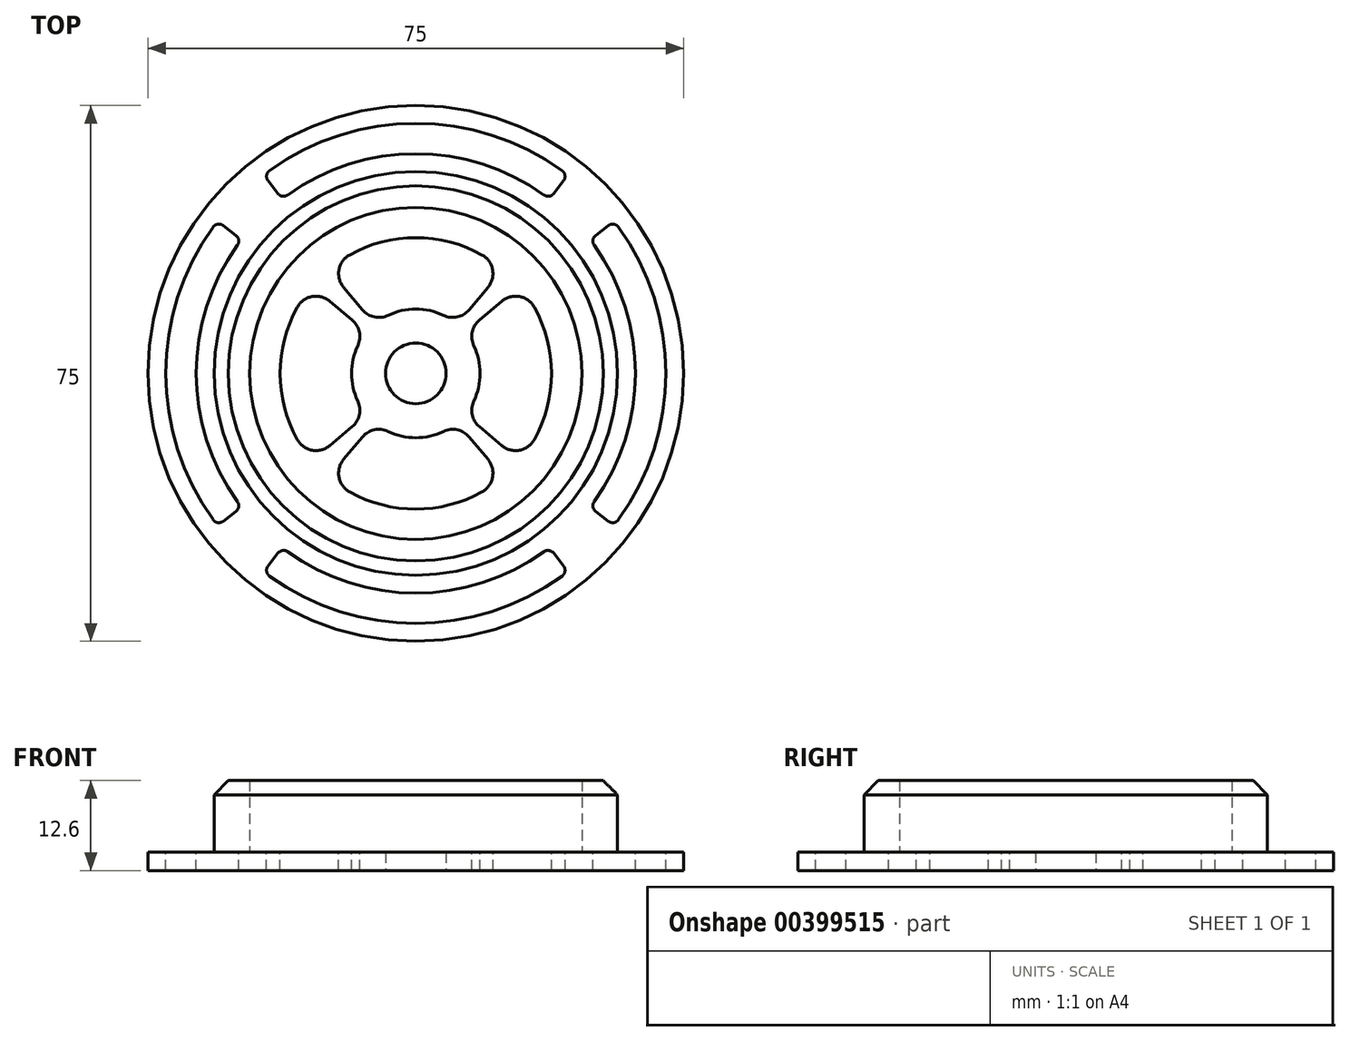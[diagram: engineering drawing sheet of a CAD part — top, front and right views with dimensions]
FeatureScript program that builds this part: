
annotation { "Feature Type Name" : "Feature", "Feature Type Description" : "" }
export const myFeature = defineFeature(function(context is Context, id is Id, definition is map)
    precondition{}
    {
        {
            var Q0;
            Q0=qCreatedBy(makeId("Top.planeOp"),FACE);
            var sketch = newSketch(context, id + "F0", { "sketchPlane" : qUnion([Q0])});
            skCircle(sketch, "E0", {"center": v(0, 0) * mm, "radius": 37.5 * mm});
            skCircle(sketch, "E1", {"center": v(0, 0) * mm, "radius": 23.25 * mm});
            skSolve(sketch);
        }
        {
            var Q0;
            Q0=makeQuery(id+"F0.imprint","IMPRINT",FACE,{"disambiguationData":[TD([[makeQuery(id+"F0.imprint","IMPRINT",EDGE,{"derivedFrom":sQuery(id+"F0.wireOp",EDGE,"E0")}),1.0]])]});
            extrude(context, id + "F1", {"entities" : qUnion([Q0]), "depth" : 2.6 * mm});
        }
        {
            var Q0;
            Q0=makeQuery(id+"F1.opExtrude","CAP_FACE",FACE,{"disambiguationData":[OSD([sQuery(id+"F0.wireOp",EDGE,"E0"),sQuery(id+"F0.wireOp",EDGE,"E1")])],"isStart":false});
            var sketch = newSketch(context, id + "F2", { "sketchPlane" : qUnion([Q0])});
            skCircle(sketch, "E2", {"center": v(0, 0) * mm, "radius": 28.25 * mm});
            skCircle(sketch, "E3", {"center": v(0, 0) * mm, "radius": 23.25 * mm});
            skSolve(sketch);
        }
        {
            var Q0;
            Q0=makeQuery(id+"F2.imprint","IMPRINT",FACE,{"disambiguationData":[TD([[makeQuery(id+"F2.imprint","IMPRINT",EDGE,{"derivedFrom":sQuery(id+"F2.wireOp",EDGE,"E2")}),1.0]])]});
            extrude(context, id + "F3", {"entities" : qUnion([Q0]), "operationType" : NewBodyOperationType.ADD, "depth" : 10 * mm});
        }
        {
            var Q0;
            Q0=makeQuery(id+"F3.opExtrude","CAP_EDGE",EDGE,{"disambiguationData":[OSD([sQuery(id+"F2.wireOp",EDGE,"E2")])],"isStart":false});
            chamfer(context, id + "F4", {"entities" : qUnion([Q0]), "width" : 2 * mm, "tangentPropagation" : true});
        }
        {
            var Q0;
            Q0=qCreatedBy(makeId("Top.planeOp"),FACE);
            var sketch = newSketch(context, id + "F5", { "sketchPlane" : qUnion([Q0])});
            skCircle(sketch, "E4", {"center": v(0, 0) * mm, "radius": 4.25 * mm});
            skCircle(sketch, "E5", {"center": v(0, 0) * mm, "radius": 23.25 * mm});
            skSolve(sketch);
        }
        {
            var Q0;
            Q0=makeQuery(id+"F5.imprint","IMPRINT",FACE,{"disambiguationData":[TD([[makeQuery(id+"F5.imprint","IMPRINT",EDGE,{"derivedFrom":sQuery(id+"F5.wireOp",EDGE,"E4")}),-1.0]])]});
            extrude(context, id + "F6", {"entities" : qUnion([Q0]), "operationType" : NewBodyOperationType.ADD, "depth" : 2.6 * mm});
        }
        {
            var Q0;
            Q0=makeQuery(id+"F6.opExtrude","CAP_FACE",FACE,{"disambiguationData":[OSD([sQuery(id+"F5.wireOp",EDGE,"E4"),sQuery(id+"F5.wireOp",EDGE,"E5")])],"isStart":false});
            var sketch = newSketch(context, id + "F7", { "sketchPlane" : qUnion([Q0])});
            skArc(sketch, "E6", {"start": v(3.88, 8.12) * mm, "mid": v(0, 9) * mm, "end": v(-3.88, 8.12) * mm});
            skArc(sketch, "E7", {"start": v(9.27, 16.59) * mm, "mid": v(0, 19) * mm, "end": v(-9.27, 16.59) * mm});
            skLineSegment(sketch, "E8", {"start": v(-7.47, 8.9) * mm, "end": v(-10.1, 12.04) * mm});
            skLineSegment(sketch, "E9", {"start": v(7.47, 8.9) * mm, "end": v(10.1, 12.04) * mm});
            skPoint(sketch, "E10.visualSharp", {"position": v(-12.21, 14.55) * mm});
            skArc(sketch, "E10.filletArc", {"start": v(-11.98, 14.75) * mm, "mid": v(-12.09, 14.54) * mm, "end": v(-12.02, 14.32) * mm});
            skArc(sketch, "E11.filletArc", {"start": v(-9.27, 16.59) * mm, "mid": v(-10.75, 14.5) * mm, "end": v(-10.1, 12.04) * mm});
            skPoint(sketch, "E12.visualSharp", {"position": v(-5.79, 6.9) * mm});
            skArc(sketch, "E12.filletArc", {"start": v(-7.47, 8.9) * mm, "mid": v(-5.8, 7.9) * mm, "end": v(-3.88, 8.12) * mm});
            skPoint(sketch, "E13.visualSharp", {"position": v(5.79, 6.9) * mm});
            skArc(sketch, "E13.filletArc", {"start": v(3.88, 8.12) * mm, "mid": v(5.8, 7.9) * mm, "end": v(7.47, 8.9) * mm});
            skPoint(sketch, "E14.visualSharp", {"position": v(12.21, 14.55) * mm});
            skArc(sketch, "E14.filletArc", {"start": v(10.1, 12.04) * mm, "mid": v(10.75, 14.5) * mm, "end": v(9.27, 16.59) * mm});
            skPoint(sketch, "E15.1.0", {"position": v(-6.9, -5.79) * mm});
            skArc(sketch, "E15.1.1", {"start": v(-12.04, 10.1) * mm, "mid": v(-14.5, 10.75) * mm, "end": v(-16.59, 9.27) * mm});
            skPoint(sketch, "E15.1.2", {"position": v(-14.55, 12.21) * mm});
            skPoint(sketch, "E15.1.3", {"position": v(-14.55, -12.21) * mm});
            skArc(sketch, "E15.1.4", {"start": v(-16.59, -9.27) * mm, "mid": v(-14.5, -10.75) * mm, "end": v(-12.04, -10.1) * mm});
            skArc(sketch, "E15.1.5", {"start": v(-8.12, 3.88) * mm, "mid": v(-9, 0) * mm, "end": v(-8.12, -3.88) * mm});
            skPoint(sketch, "E15.1.6", {"position": v(-6.9, 5.79) * mm});
            skArc(sketch, "E15.1.7", {"start": v(-16.59, 9.27) * mm, "mid": v(-19, 0) * mm, "end": v(-16.59, -9.27) * mm});
            skLineSegment(sketch, "E15.1.8", {"start": v(-8.9, 7.47) * mm, "end": v(-12.04, 10.1) * mm});
            skLineSegment(sketch, "E15.1.9", {"start": v(-8.9, -7.47) * mm, "end": v(-12.04, -10.1) * mm});
            skArc(sketch, "E15.1.10", {"start": v(-8.12, 3.88) * mm, "mid": v(-7.9, 5.8) * mm, "end": v(-8.9, 7.47) * mm});
            skArc(sketch, "E15.1.11", {"start": v(-8.9, -7.47) * mm, "mid": v(-7.9, -5.8) * mm, "end": v(-8.12, -3.88) * mm});
            skArc(sketch, "E15.1.12", {"start": v(-14.75, -11.98) * mm, "mid": v(-14.54, -12.09) * mm, "end": v(-14.32, -12.02) * mm});
            skPoint(sketch, "E15.2.0", {"position": v(5.79, -6.9) * mm});
            skArc(sketch, "E15.2.1", {"start": v(-10.1, -12.04) * mm, "mid": v(-10.75, -14.5) * mm, "end": v(-9.27, -16.59) * mm});
            skPoint(sketch, "E15.2.2", {"position": v(-12.21, -14.55) * mm});
            skPoint(sketch, "E15.2.3", {"position": v(12.21, -14.55) * mm});
            skArc(sketch, "E15.2.4", {"start": v(9.27, -16.59) * mm, "mid": v(10.75, -14.5) * mm, "end": v(10.1, -12.04) * mm});
            skArc(sketch, "E15.2.5", {"start": v(-3.88, -8.12) * mm, "mid": v(0, -9) * mm, "end": v(3.88, -8.12) * mm});
            skPoint(sketch, "E15.2.6", {"position": v(-5.79, -6.9) * mm});
            skArc(sketch, "E15.2.7", {"start": v(-9.27, -16.59) * mm, "mid": v(0, -19) * mm, "end": v(9.27, -16.59) * mm});
            skLineSegment(sketch, "E15.2.8", {"start": v(-7.47, -8.9) * mm, "end": v(-10.1, -12.04) * mm});
            skLineSegment(sketch, "E15.2.9", {"start": v(7.47, -8.9) * mm, "end": v(10.1, -12.04) * mm});
            skArc(sketch, "E15.2.10", {"start": v(-3.88, -8.12) * mm, "mid": v(-5.8, -7.9) * mm, "end": v(-7.47, -8.9) * mm});
            skArc(sketch, "E15.2.11", {"start": v(7.47, -8.9) * mm, "mid": v(5.8, -7.9) * mm, "end": v(3.88, -8.12) * mm});
            skArc(sketch, "E15.2.12", {"start": v(11.98, -14.75) * mm, "mid": v(12.09, -14.54) * mm, "end": v(12.02, -14.32) * mm});
            skPoint(sketch, "E15.3.0", {"position": v(6.9, 5.79) * mm});
            skArc(sketch, "E15.3.1", {"start": v(12.04, -10.1) * mm, "mid": v(14.5, -10.75) * mm, "end": v(16.59, -9.27) * mm});
            skPoint(sketch, "E15.3.2", {"position": v(14.55, -12.21) * mm});
            skPoint(sketch, "E15.3.3", {"position": v(14.55, 12.21) * mm});
            skArc(sketch, "E15.3.4", {"start": v(16.59, 9.27) * mm, "mid": v(14.5, 10.75) * mm, "end": v(12.04, 10.1) * mm});
            skArc(sketch, "E15.3.5", {"start": v(8.12, -3.88) * mm, "mid": v(9, 0) * mm, "end": v(8.12, 3.88) * mm});
            skPoint(sketch, "E15.3.6", {"position": v(6.9, -5.79) * mm});
            skArc(sketch, "E15.3.7", {"start": v(16.59, -9.27) * mm, "mid": v(19, 0) * mm, "end": v(16.59, 9.27) * mm});
            skLineSegment(sketch, "E15.3.8", {"start": v(8.9, -7.47) * mm, "end": v(12.04, -10.1) * mm});
            skLineSegment(sketch, "E15.3.9", {"start": v(8.9, 7.47) * mm, "end": v(12.04, 10.1) * mm});
            skArc(sketch, "E15.3.10", {"start": v(8.12, -3.88) * mm, "mid": v(7.9, -5.8) * mm, "end": v(8.9, -7.47) * mm});
            skArc(sketch, "E15.3.11", {"start": v(8.9, 7.47) * mm, "mid": v(7.9, 5.8) * mm, "end": v(8.12, 3.88) * mm});
            skArc(sketch, "E15.3.12", {"start": v(14.75, 11.98) * mm, "mid": v(14.54, 12.09) * mm, "end": v(14.32, 12.02) * mm});
            skSolve(sketch);
        }
        {
            var Q0;
            Q0=makeQuery(id+"F7.imprint","IMPRINT",FACE,{"disambiguationData":[TD([[makeQuery(id+"F7.imprint","IMPRINT",EDGE,{"derivedFrom":sQuery(id+"F7.wireOp",EDGE,"E6")}),-1.0]])]});
            var Q1;
            Q1=makeQuery(id+"F7.imprint","IMPRINT",FACE,{"disambiguationData":[TD([[makeQuery(id+"F7.imprint","IMPRINT",EDGE,{"derivedFrom":sQuery(id+"F7.wireOp",EDGE,"E15.3.1")}),1.0]])]});
            var Q2;
            Q2=makeQuery(id+"F7.imprint","IMPRINT",FACE,{"disambiguationData":[TD([[makeQuery(id+"F7.imprint","IMPRINT",EDGE,{"derivedFrom":sQuery(id+"F7.wireOp",EDGE,"E15.2.1")}),1.0]])]});
            var Q3;
            Q3=makeQuery(id+"F7.imprint","IMPRINT",FACE,{"disambiguationData":[TD([[makeQuery(id+"F7.imprint","IMPRINT",EDGE,{"derivedFrom":sQuery(id+"F7.wireOp",EDGE,"E15.1.1")}),1.0]])]});
            extrude(context, id + "F8", {"entities" : qUnion([Q0, Q1, Q2, Q3]), "operationType" : NewBodyOperationType.REMOVE, "endBound" : BoundingType.THROUGH_ALL, "oppositeDirection" : true, "depth" : 25 * mm});
        }
        {
            var Q0;
            Q0=makeQuery(id+"F1.opExtrude","CAP_FACE",FACE,{"disambiguationData":[OSD([sQuery(id+"F0.wireOp",EDGE,"E0"),sQuery(id+"F0.wireOp",EDGE,"E1")])],"isStart":false});
            var sketch = newSketch(context, id + "F9", { "sketchPlane" : qUnion([Q0])});
            skArc(sketch, "E16", {"start": v(20.48, 28.38) * mm, "mid": v(0, 35) * mm, "end": v(-20.48, 28.38) * mm});
            skArc(sketch, "E17", {"start": v(17.94, 24.97) * mm, "mid": v(0, 30.75) * mm, "end": v(-17.94, 24.97) * mm});
            skLineSegment(sketch, "E18", {"start": v(-19.32, 25.18) * mm, "end": v(-20.69, 26.96) * mm});
            skLineSegment(sketch, "E19", {"start": v(19.32, 25.18) * mm, "end": v(20.69, 26.96) * mm});
            skPoint(sketch, "E20.visualSharp", {"position": v(-21.3, 27.77) * mm});
            skArc(sketch, "E20.filletArc", {"start": v(-20.48, 28.38) * mm, "mid": v(-20.88, 27.72) * mm, "end": v(-20.69, 26.96) * mm});
            skPoint(sketch, "E21.visualSharp", {"position": v(-18.72, 24.4) * mm});
            skArc(sketch, "E21.filletArc", {"start": v(-19.32, 25.18) * mm, "mid": v(-18.67, 24.8) * mm, "end": v(-17.94, 24.97) * mm});
            skPoint(sketch, "E22.visualSharp", {"position": v(18.72, 24.4) * mm});
            skArc(sketch, "E22.filletArc", {"start": v(17.94, 24.97) * mm, "mid": v(18.67, 24.8) * mm, "end": v(19.32, 25.18) * mm});
            skPoint(sketch, "E23.visualSharp", {"position": v(21.3, 27.77) * mm});
            skArc(sketch, "E23.filletArc", {"start": v(20.69, 26.96) * mm, "mid": v(20.88, 27.72) * mm, "end": v(20.48, 28.38) * mm});
            skPoint(sketch, "E24.1.0", {"position": v(-24.4, 18.72) * mm});
            skPoint(sketch, "E24.1.1", {"position": v(-24.4, -18.72) * mm});
            skPoint(sketch, "E24.1.2", {"position": v(-27.77, 21.3) * mm});
            skPoint(sketch, "E24.1.3", {"position": v(-27.77, -21.3) * mm});
            skArc(sketch, "E24.1.4", {"start": v(-28.38, 20.48) * mm, "mid": v(-35, 0) * mm, "end": v(-28.38, -20.48) * mm});
            skArc(sketch, "E24.1.5", {"start": v(-24.97, 17.94) * mm, "mid": v(-30.75, 0) * mm, "end": v(-24.97, -17.94) * mm});
            skArc(sketch, "E24.1.6", {"start": v(-25.18, -19.32) * mm, "mid": v(-24.8, -18.67) * mm, "end": v(-24.97, -17.94) * mm});
            skArc(sketch, "E24.1.7", {"start": v(-26.96, 20.69) * mm, "mid": v(-27.72, 20.88) * mm, "end": v(-28.38, 20.48) * mm});
            skArc(sketch, "E24.1.8", {"start": v(-24.97, 17.94) * mm, "mid": v(-24.8, 18.67) * mm, "end": v(-25.18, 19.32) * mm});
            skArc(sketch, "E24.1.9", {"start": v(-28.38, -20.48) * mm, "mid": v(-27.72, -20.88) * mm, "end": v(-26.96, -20.69) * mm});
            skLineSegment(sketch, "E24.1.10", {"start": v(-25.18, 19.32) * mm, "end": v(-26.96, 20.69) * mm});
            skLineSegment(sketch, "E24.1.11", {"start": v(-25.18, -19.32) * mm, "end": v(-26.96, -20.69) * mm});
            skPoint(sketch, "E24.2.0", {"position": v(-18.72, -24.4) * mm});
            skPoint(sketch, "E24.2.1", {"position": v(18.72, -24.4) * mm});
            skPoint(sketch, "E24.2.2", {"position": v(-21.3, -27.77) * mm});
            skPoint(sketch, "E24.2.3", {"position": v(21.3, -27.77) * mm});
            skArc(sketch, "E24.2.4", {"start": v(-20.48, -28.38) * mm, "mid": v(0, -35) * mm, "end": v(20.48, -28.38) * mm});
            skArc(sketch, "E24.2.5", {"start": v(-17.94, -24.97) * mm, "mid": v(0, -30.75) * mm, "end": v(17.94, -24.97) * mm});
            skArc(sketch, "E24.2.6", {"start": v(19.32, -25.18) * mm, "mid": v(18.67, -24.8) * mm, "end": v(17.94, -24.97) * mm});
            skArc(sketch, "E24.2.7", {"start": v(-20.69, -26.96) * mm, "mid": v(-20.88, -27.72) * mm, "end": v(-20.48, -28.38) * mm});
            skArc(sketch, "E24.2.8", {"start": v(-17.94, -24.97) * mm, "mid": v(-18.67, -24.8) * mm, "end": v(-19.32, -25.18) * mm});
            skArc(sketch, "E24.2.9", {"start": v(20.48, -28.38) * mm, "mid": v(20.88, -27.72) * mm, "end": v(20.69, -26.96) * mm});
            skLineSegment(sketch, "E24.2.10", {"start": v(-19.32, -25.18) * mm, "end": v(-20.69, -26.96) * mm});
            skLineSegment(sketch, "E24.2.11", {"start": v(19.32, -25.18) * mm, "end": v(20.69, -26.96) * mm});
            skPoint(sketch, "E24.3.0", {"position": v(24.4, -18.72) * mm});
            skPoint(sketch, "E24.3.1", {"position": v(24.4, 18.72) * mm});
            skPoint(sketch, "E24.3.2", {"position": v(27.77, -21.3) * mm});
            skPoint(sketch, "E24.3.3", {"position": v(27.77, 21.3) * mm});
            skArc(sketch, "E24.3.4", {"start": v(28.38, -20.48) * mm, "mid": v(35, 0) * mm, "end": v(28.38, 20.48) * mm});
            skArc(sketch, "E24.3.5", {"start": v(24.97, -17.94) * mm, "mid": v(30.75, 0) * mm, "end": v(24.97, 17.94) * mm});
            skArc(sketch, "E24.3.6", {"start": v(25.18, 19.32) * mm, "mid": v(24.8, 18.67) * mm, "end": v(24.97, 17.94) * mm});
            skArc(sketch, "E24.3.7", {"start": v(26.96, -20.69) * mm, "mid": v(27.72, -20.88) * mm, "end": v(28.38, -20.48) * mm});
            skArc(sketch, "E24.3.8", {"start": v(24.97, -17.94) * mm, "mid": v(24.8, -18.67) * mm, "end": v(25.18, -19.32) * mm});
            skArc(sketch, "E24.3.9", {"start": v(28.38, 20.48) * mm, "mid": v(27.72, 20.88) * mm, "end": v(26.96, 20.69) * mm});
            skLineSegment(sketch, "E24.3.10", {"start": v(25.18, -19.32) * mm, "end": v(26.96, -20.69) * mm});
            skLineSegment(sketch, "E24.3.11", {"start": v(25.18, 19.32) * mm, "end": v(26.96, 20.69) * mm});
            skSolve(sketch);
        }
        {
            var Q0;
            Q0=makeQuery(id+"F9.imprint","IMPRINT",FACE,{"disambiguationData":[TD([[makeQuery(id+"F9.imprint","IMPRINT",EDGE,{"derivedFrom":sQuery(id+"F9.wireOp",EDGE,"E16")}),1.0]])]});
            var Q1;
            Q1=makeQuery(id+"F9.imprint","IMPRINT",FACE,{"disambiguationData":[TD([[makeQuery(id+"F9.imprint","IMPRINT",EDGE,{"derivedFrom":sQuery(id+"F9.wireOp",EDGE,"E24.3.4")}),1.0]])]});
            var Q2;
            Q2=makeQuery(id+"F9.imprint","IMPRINT",FACE,{"disambiguationData":[TD([[makeQuery(id+"F9.imprint","IMPRINT",EDGE,{"derivedFrom":sQuery(id+"F9.wireOp",EDGE,"E24.2.4")}),1.0]])]});
            var Q3;
            Q3=makeQuery(id+"F9.imprint","IMPRINT",FACE,{"disambiguationData":[TD([[makeQuery(id+"F9.imprint","IMPRINT",EDGE,{"derivedFrom":sQuery(id+"F9.wireOp",EDGE,"E24.1.4")}),1.0]])]});
            extrude(context, id + "F10", {"entities" : qUnion([Q0, Q1, Q2, Q3]), "operationType" : NewBodyOperationType.REMOVE, "endBound" : BoundingType.THROUGH_ALL, "oppositeDirection" : true, "depth" : 25 * mm});
        }
    });
